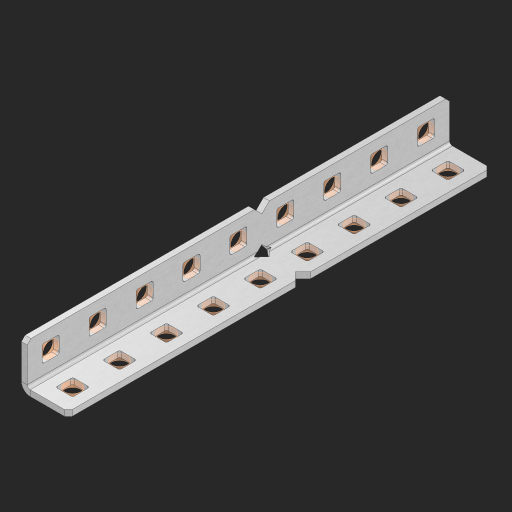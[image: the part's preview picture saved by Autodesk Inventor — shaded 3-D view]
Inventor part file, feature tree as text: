
AUTODESK INVENTOR PART (.ipt)
format: ipt  version: 2023 (Build 270158000, 158)  size: 577,536 bytes
history: native  units: in
note: dims shown in document units (in); Inventor stores cm internally (conversion verified against a paired STEP export)
features: other x24, extrude x19, sheet_metal_op x8, sketch x5, pattern_linear x1, mirror x1, chamfer x1
ambient origin geometry x8: Origin, YZ Plane, XZ Plane, XY Plane, X Axis, Y Axis, Z Axis, Center Point
bodies: Solid1 (feature_tree), Body (feature_tree)
feature tree (59):
  sheet_metal_op  "Flanges"
  sheet_metal_op  "Body Pattern"
  other  "Arc Length"
  pattern_linear  "Notch Pattern"  Spacing1=0.125in  [1 undecoded]
  other  "Diagonal Plane"
  mirror  "Everything Mirrored"
  chamfer  "End Chamfer"
  sketch  "Sketch1"  dims[d0=0.5in]
  other  "Plate1"
  sketch  "Sketch2"  dims[d1=4.5in]
  other  "Plate2"
  sheet_metal_op  "Bend1"
  sheet_metal_op  "Corner1"
  sketch  "Sketch8"  dims[d2=0.0625in]
  sketch  "Sketch9"  dims[d3=0.0625in]
  other  "Srf91"
  sheet_metal_op  "Body Pattern Sketch"
  other  "Srf92"
  sketch  "Sketch13"  dims[d4=0.0312in d5=0.125in d6=0.0625in d7=0.5in d8=90.0deg d9=0.0312in d10=0.25in d11=0.0625in d12=0.0625in d49=0.182in d50=0.02in d52=0.25in d53=0.0625in d54=0.0in d55=0.172in d56=1.0in d57=0.0in d85=0.1473in d86=0.1782in d89=0.0625in d90=0.0in d91=0.04in d92=0.0491in d95=2.5in d96=0.04in d97=0.25in d98=45.0deg d123=0.204in d126=0.0491in d127=0.1473in d128=0.08in d129=0.04in d130=2.5in d131=3.5433in d133=0.5in d134=0.3937in d136=1.0in]
  other  "Srf856"
  other  "Srf857"
  other  "Srf858"
  other  "Srf859"
  other  "Srf860"
  other  "Srf861"
  other  "Srf1275"
  other  "Srf1276"
  other  "Srf1278"
  other  "Srf1279"
  other  "Srf1280"
  other  "Srf1281"
  other  "Srf1282"
  other  "Srf1283"
  other  "Srf1383"
  other  "Srf1384"
  other  "Srf1475"
  other  "Srf1476"
  sheet_metal_op  "Body Stamp"
  sheet_metal_op  "Body Circle"
  sheet_metal_op  "Notch"
  extrude  "ExtrusionSrf92"  Depth=0.0625in
  extrude  "ExtrusionSrf856"  Depth=0.5in TaperAngle=90.0deg
  extrude  "ExtrusionSrf857"  Depth=0.3937in
  extrude  "ExtrusionSrf858"  Depth=0.0625in
  extrude  "ExtrusionSrf859"  Depth=0.0625in
  extrude  "ExtrusionSrf860"  Depth=0.3937in
  extrude  "ExtrusionSrf861"  Depth=0.02in
  extrude  "ExtrusionSrf1275"  Depth=0.3937in
  extrude  "ExtrusionSrf1276"  Depth=0.0625in
  extrude  "ExtrusionSrf1277"  TaperAngle=0.0deg  [1 undecoded]
  extrude  "ExtrusionSrf1278"  Depth=0.3937in
  extrude  "ExtrusionSrf1279"  Depth=0.3937in TaperAngle=0.0deg
  extrude  "ExtrusionSrf1280"  Depth=0.3937in
  extrude  "ExtrusionSrf1281"  Depth=0.3937in
  extrude  "ExtrusionSrf1282"  Depth=0.0625in
  extrude  "ExtrusionSrf1383"  Depth=0.3937in TaperAngle=0.0deg
  extrude  "ExtrusionSrf1384"  Depth=0.3937in
  extrude  "ExtrusionSrf1475"  Depth=0.3937in TaperAngle=45.0deg
  extrude  "ExtrusionSrf1476"  Depth=0.3937in
note: 2 required parameter values undecoded (feature->parameter linkage not recoverable at this tier; creation-order binding heuristic only, values carry confidence <= 0.55)
